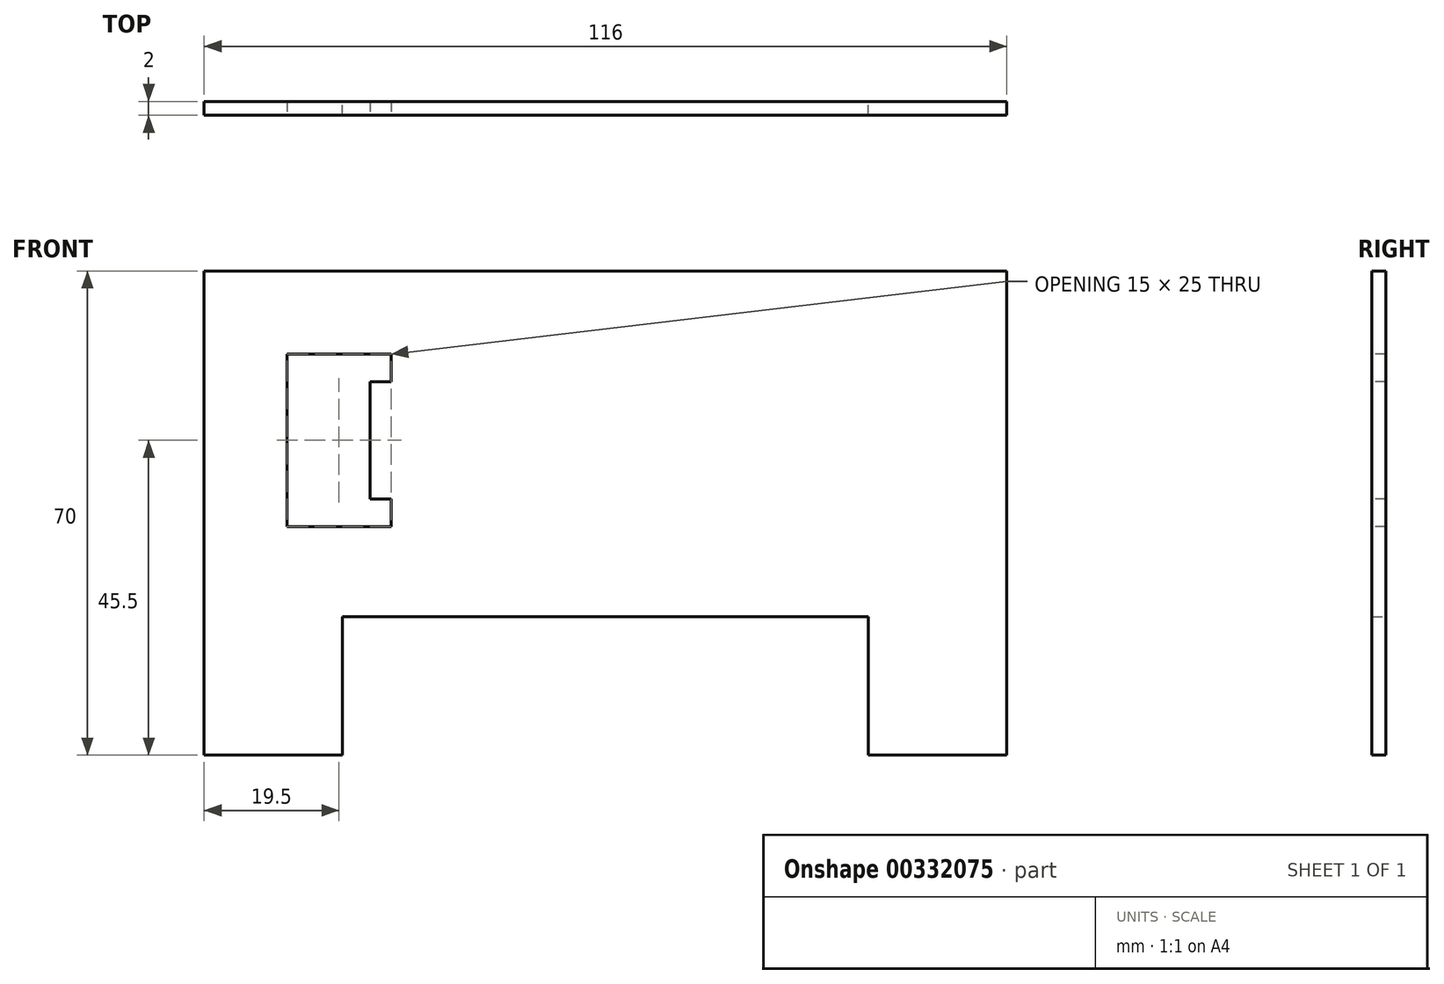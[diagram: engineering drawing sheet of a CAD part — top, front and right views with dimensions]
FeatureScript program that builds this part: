
annotation { "Feature Type Name" : "Feature", "Feature Type Description" : "" }
export const myFeature = defineFeature(function(context is Context, id is Id, definition is map)
    precondition{}
    {
        {
            var Q0;
            Q0=qCreatedBy(makeId("Front.planeOp"),FACE);
            var sketch = newSketch(context, id + "F0", { "sketchPlane" : qUnion([Q0])});
            skLineSegment(sketch, "E0", {"start": v(0, 0) * mm, "end": v(-20, 0) * mm});
            skLineSegment(sketch, "E1", {"start": v(-20, 0) * mm, "end": v(-20, 20) * mm});
            skLineSegment(sketch, "E2", {"start": v(-20, 20) * mm, "end": v(-96, 20) * mm});
            skLineSegment(sketch, "E3", {"start": v(-96, 20) * mm, "end": v(-96, 0) * mm});
            skLineSegment(sketch, "E4", {"start": v(-96, 0) * mm, "end": v(-116, 0) * mm});
            skLineSegment(sketch, "E5", {"start": v(-116, 0) * mm, "end": v(-116, 70) * mm});
            skLineSegment(sketch, "E6", {"start": v(-116, 70) * mm, "end": v(0, 70) * mm});
            skLineSegment(sketch, "E7", {"start": v(0, 0) * mm, "end": v(0, 70) * mm});
            skSolve(sketch);
        }
        {
            var Q0;
            Q0=makeQuery(id+"F0.imprint","IMPRINT",FACE,{"disambiguationData":[TD([[makeQuery(id+"F0.imprint","IMPRINT",EDGE,{"derivedFrom":sQuery(id+"F0.wireOp",EDGE,"E0")}),-1.0]])]});
            extrude(context, id + "F1", {"entities" : qUnion([Q0]), "depth" : 2 * mm});
        }
        {
            var Q0;
            Q0=makeQuery(id+"F1.opExtrude","CAP_FACE",FACE,{"disambiguationData":[OSD([sQuery(id+"F0.wireOp",EDGE,"E0"),sQuery(id+"F0.wireOp",EDGE,"E1"),sQuery(id+"F0.wireOp",EDGE,"E2"),sQuery(id+"F0.wireOp",EDGE,"E3"),sQuery(id+"F0.wireOp",EDGE,"E4"),sQuery(id+"F0.wireOp",EDGE,"E5"),sQuery(id+"F0.wireOp",EDGE,"E6"),sQuery(id+"F0.wireOp",EDGE,"E7")])],"isStart":false});
            var sketch = newSketch(context, id + "F2", { "sketchPlane" : qUnion([Q0])});
            skLineSegment(sketch, "E8", {"start": v(-104, 58) * mm, "end": v(-104, 33) * mm});
            skLineSegment(sketch, "E9", {"start": v(-104, 33) * mm, "end": v(-89, 33) * mm});
            skLineSegment(sketch, "E10", {"start": v(-89, 33) * mm, "end": v(-89, 37) * mm});
            skLineSegment(sketch, "E11", {"start": v(-89, 37) * mm, "end": v(-92, 37) * mm});
            skLineSegment(sketch, "E12", {"start": v(-92, 37) * mm, "end": v(-92, 54) * mm});
            skLineSegment(sketch, "E13", {"start": v(-92, 54) * mm, "end": v(-89, 54) * mm});
            skLineSegment(sketch, "E14", {"start": v(-89, 54) * mm, "end": v(-89, 58) * mm});
            skLineSegment(sketch, "E15", {"start": v(-89, 58) * mm, "end": v(-104, 58) * mm});
            skSolve(sketch);
        }
        {
            var Q0;
            Q0 = qSketchRegion(id + "F2", true);
            extrude(context, id + "F3", {"entities" : qUnion([Q0]), "operationType" : NewBodyOperationType.REMOVE, "endBound" : BoundingType.THROUGH_ALL, "oppositeDirection" : true, "depth" : 25 * mm, "offsetDistance" : 25 * mm});
        }
    });
